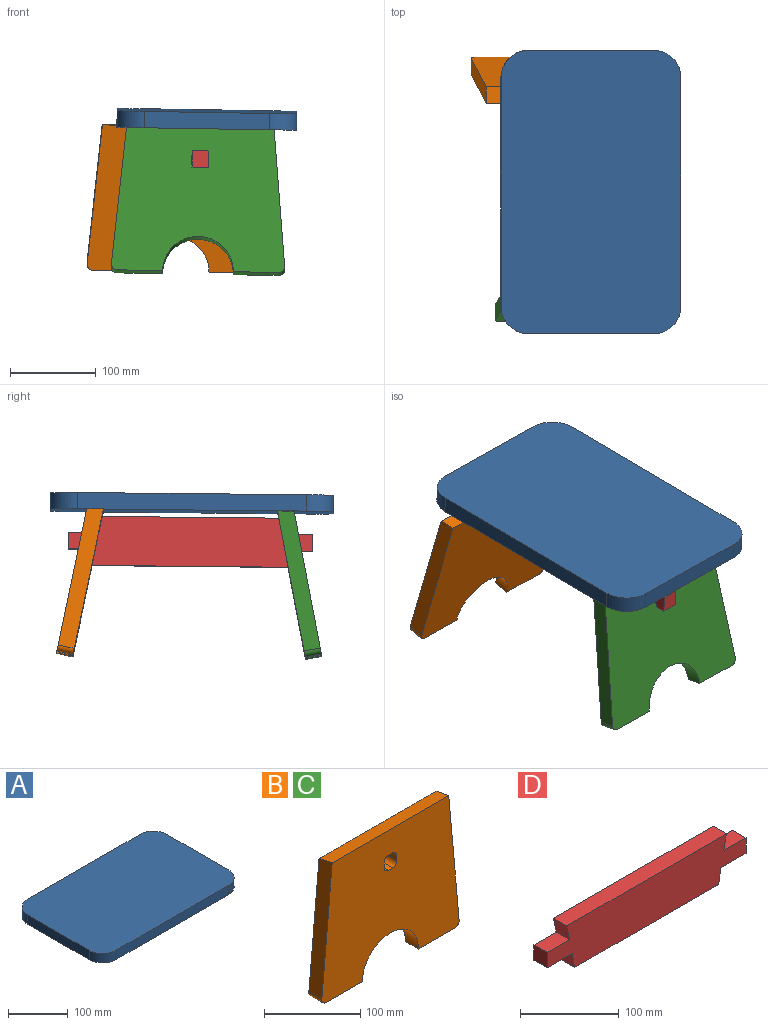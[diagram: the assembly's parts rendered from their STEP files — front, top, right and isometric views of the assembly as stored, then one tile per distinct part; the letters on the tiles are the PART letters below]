
ASSEMBLY  parts=4 mates=4
PART A: 10 faces, bbox 330.2x209.6x19.1 mm
  f0: plane 146.05x19.05mm, normal (-1,0,0), area 2782.3mm2, adj f1,f7,f8,f9
  f1: cylinder r=31.75mm len=31.75mm, axis (0,0,-1), area 950.1mm2, adj f0,f2,f8,f9
  f2: plane 266.7x19.05mm, normal (0,-1,0), area 5080.6mm2, adj f1,f3,f8,f9
  f3: cylinder r=31.75mm len=31.75mm, axis (0,0,-1), area 950.1mm2, adj f2,f4,f8,f9
  f4: plane 146.05x19.05mm, normal (1,0,0), area 2782.3mm2, adj f3,f5,f8,f9
  f5: cylinder r=31.75mm len=31.75mm, axis (0,0,-1), area 950.1mm2, adj f4,f6,f8,f9
  f6: plane 266.7x19.05mm, normal (0,1,0), area 5080.6mm2, adj f5,f7,f8,f9
  f7: cylinder r=31.75mm len=31.75mm, axis (0,0,-1), area 950.1mm2, adj f0,f6,f8,f9
  f8: plane 330.2x209.55mm, normal (0,0,1), area 68328.1mm2, adj f0,f1,f2,f3,f4,f5,f6,f7
  f9: plane 330.2x209.55mm, normal (0,0,-1), area 68328.1mm2, adj f0,f1,f2,f3,f4,f5,f6,f7
PART B: 18 faces, bbox 202x19.1x173.3 mm
  f0: plane 166.36x19.05mm, normal (-1,0,0.09), area 3146mm2, adj f1,f15,f16,f17
  f1: cylinder r=6.35mm len=19.05mm, axis (0,1,0), area 201.1mm2, adj f0,f2,f15,f16
  f2: plane 53.37x19.05mm, normal (0,0,-1), area 1016.6mm2, adj f1,f3,f15,f16
  f3: cylinder r=41.27mm len=82.55mm, axis (0,1,0), area 2470.2mm2, adj f2,f4,f15,f16
  f4: plane 53.37x19.05mm, normal (0,0,-1), area 1016.6mm2, adj f3,f5,f15,f16
  f5: cylinder r=6.35mm len=19.05mm, axis (0,1,0), area 201.1mm2, adj f4,f6,f15,f16
  f6: plane 166.36x19.05mm, normal (1,0,0.09), area 3146mm2, adj f5,f15,f16,f17
  f7: cylinder r=6.35mm len=19.05mm, axis (0,1,0), area 190mm2, adj f8,f14,f15,f16
  f8: plane 19.05x6.35mm, normal (0,0,-1), area 121mm2, adj f7,f9,f15,f16
  f9: cylinder r=6.35mm len=19.05mm, axis (0,1,0), area 190mm2, adj f8,f10,f15,f16
  f10: plane 19.05x6.35mm, normal (-1,0,0), area 121mm2, adj f9,f11,f15,f16
  f11: cylinder r=6.35mm len=19.05mm, axis (0,1,0), area 190mm2, adj f10,f12,f15,f16
  f12: plane 19.05x6.35mm, normal (0,0,1), area 121mm2, adj f11,f13,f15,f16
  f13: cylinder r=6.35mm len=19.05mm, axis (0,1,0), area 190mm2, adj f12,f14,f15,f16
  f14: plane 19.05x6.35mm, normal (1,0,0), area 121mm2, adj f7,f13,f15,f16
  f15: plane 201.98x173.29mm, normal (0,-1,0), area 29436.1mm2, adj f0,f1,f2,f3,f4,f5,f6,f7
  f16: plane 201.98x169.48mm, normal (0,1,0), area 28781.5mm2, adj f0,f1,f2,f3,f4,f5,f6,f7
  f17: plane 172.15x19.05mm, normal (0,0.2,0.98), area 3337.6mm2, adj f0,f6,f15,f16
PART C: same geometry as B
PART D: 14 faces, bbox 284.5x19.1x57.2 mm
  f0: plane 19.05x19.05mm, normal (0.98,0,-0.2), area 370.1mm2, adj f1,f11,f12,f13
  f1: plane 228.6x19.05mm, normal (0,0,1), area 4354.8mm2, adj f0,f2,f12,f13
  f2: plane 19.05x19.05mm, normal (-0.98,0,-0.2), area 370.1mm2, adj f1,f3,f12,f13
  f3: plane 31.75x19.05mm, normal (0,0,1), area 604.8mm2, adj f2,f4,f12,f13
  f4: plane 19.05x19.05mm, normal (-1,0,0), area 362.9mm2, adj f3,f5,f12,f13
  f5: plane 35.56x19.05mm, normal (0,0,-1), area 677.4mm2, adj f4,f6,f12,f13
  f6: plane 19.05x19.05mm, normal (-0.98,0,-0.2), area 370.1mm2, adj f5,f7,f12,f13
  f7: plane 205.74x19.05mm, normal (0,0,-1), area 3919.3mm2, adj f6,f8,f12,f13
  f8: plane 19.05x19.05mm, normal (0.98,0,-0.2), area 370.1mm2, adj f7,f9,f12,f13
  f9: plane 35.56x19.05mm, normal (0,0,-1), area 677.4mm2, adj f8,f10,f12,f13
  f10: plane 19.05x19.05mm, normal (1,0,0), area 362.9mm2, adj f9,f11,f12,f13
  f11: plane 31.75x19.05mm, normal (0,0,1), area 604.8mm2, adj f0,f10,f12,f13
  f12: plane 284.48x57.15mm, normal (0,-1,0), area 13693.5mm2, adj f0,f1,f2,f3,f4,f5,f6,f7
  f13: plane 284.48x57.15mm, normal (0,1,0), area 13693.5mm2, adj f0,f1,f2,f3,f4,f5,f6,f7
PLACE A rot(axis=(0,0.01,-1),90deg) t=(-414.31,52.23,-204.58)mm fixed
PLACE B rot(axis=(1,0.08,-0.01),11.9deg) t=(-459.44,191.74,-283.76)mm
PLACE C rot(axis=(-0.01,-0.09,-1),180deg) t=(-415.26,-82.51,-287.1)mm
PLACE D rot(axis=(-0.71,-0.71,0),179.1deg) t=(-412.21,54.14,-235.67)mm
MATE planar C.f15 <-> D.f2  axis (0,0.98,-0.19) through (-423.18,-63.2,-287.44)mm
MATE planar C.f17 <-> A.f9  axis (0.02,-0.01,1) through (-335.79,-67.13,-207)mm
MATE planar D.f8 <-> B.f15  axis (0,0.98,0.21) through (-421.47,158.78,-220.04)mm
MATE planar A.f7 <-> B.f17  axis (-0.02,0.01,-1) through (-341.28,185.58,-204.5)mm
